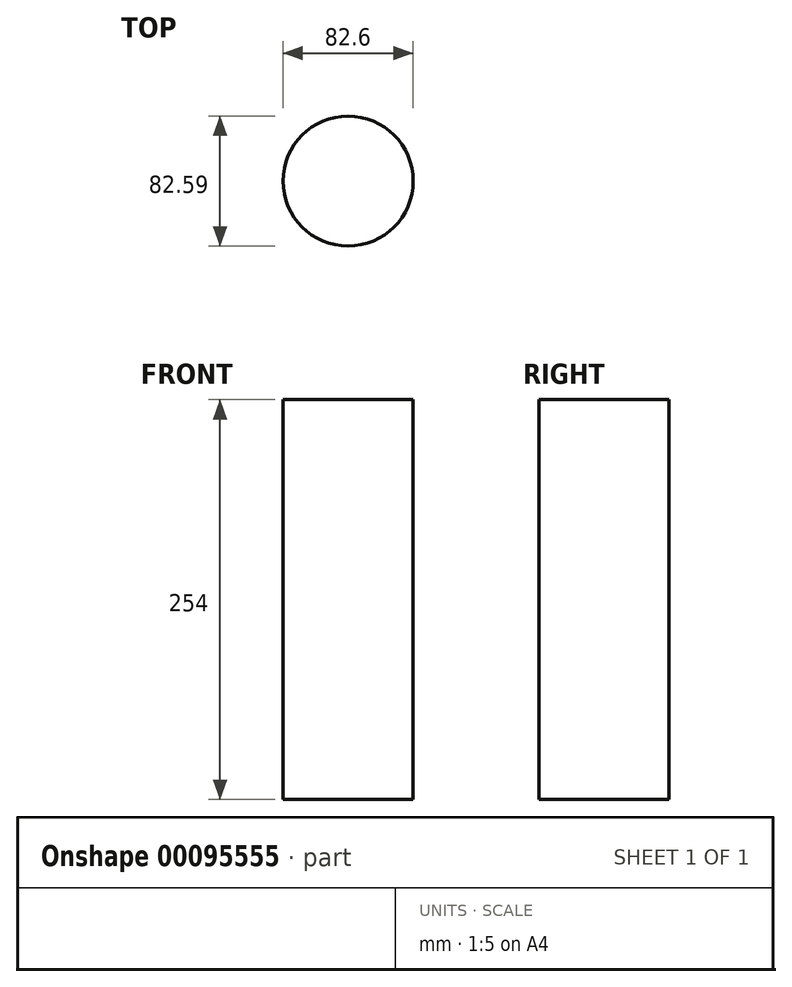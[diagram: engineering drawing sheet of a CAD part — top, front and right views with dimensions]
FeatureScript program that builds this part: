
annotation { "Feature Type Name" : "Feature", "Feature Type Description" : "" }
export const myFeature = defineFeature(function(context is Context, id is Id, definition is map)
    precondition{}
    {
        {
            var Q0;
            Q0=qCreatedBy(makeId("Top.planeOp"),FACE);
            var sketch = newSketch(context, id + "F0", { "sketchPlane" : qUnion([Q0])});
            skCircle(sketch, "E0", {"center": v(-28.11, 30.25) * mm, "radius": 41.3 * mm});
            skPoint(sketch, "E0.first.point", {"position": v(0, 0) * mm});
            skPoint(sketch, "E0.second.point", {"position": v(-63.8, 51.02) * mm});
            skPoint(sketch, "E0.third.point", {"position": v(7.06, 51.9) * mm});
            skSolve(sketch);
        }
        {
            var Q0;
            Q0 = qSketchRegion(id + "F0", true);
            extrude(context, id + "F1", {"entities" : qUnion([Q0]), "depth" : 254 * mm});
        }
    });
